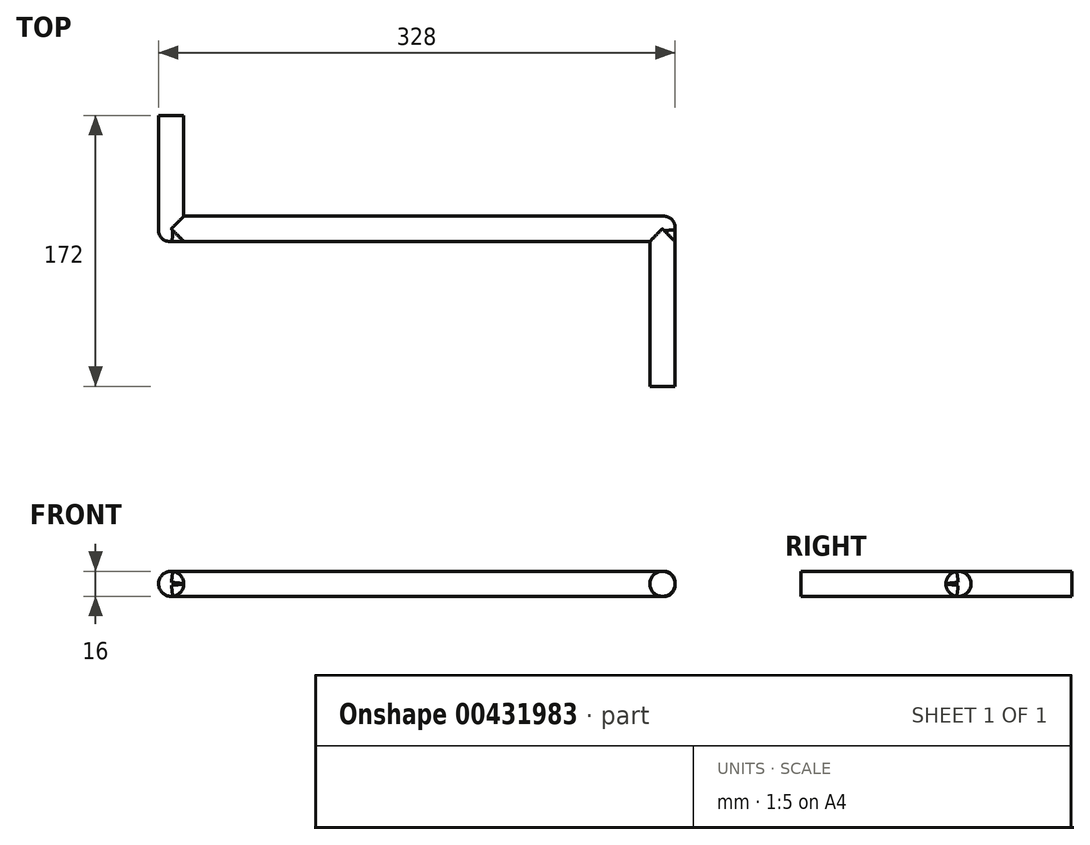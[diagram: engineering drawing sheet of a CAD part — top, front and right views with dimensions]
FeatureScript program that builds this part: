
annotation { "Feature Type Name" : "Feature", "Feature Type Description" : "" }
export const myFeature = defineFeature(function(context is Context, id is Id, definition is map)
    precondition{}
    {
        {
            var Q0;
            Q0=qCreatedBy(makeId("Front.planeOp"),FACE);
            var sketch = newSketch(context, id + "F0", { "sketchPlane" : qUnion([Q0])});
            skCircle(sketch, "E0", {"center": v(0, 0) * mm, "radius": 8 * mm});
            skSolve(sketch);
        }
        {
            var Q0;
            Q0=qSketchRegion(id+"F0",true);
            extrude(context, id + "F1", {"entities" : qUnion([Q0]), "depth" : 80 * mm});
        }
        {
            var Q0;
            Q0=qCreatedBy(makeId("Right.planeOp"),FACE);
            var sketch = newSketch(context, id + "F2", { "sketchPlane" : qUnion([Q0])});
            skCircle(sketch, "E1", {"center": v(-72, 0) * mm, "radius": 8 * mm});
            skSolve(sketch);
        }
        {
            var Q0;
            Q0=qSketchRegion(id+"F2",true);
            extrude(context, id + "F3", {"entities" : qUnion([Q0]), "operationType" : NewBodyOperationType.ADD, "depth" : 320 * mm, "offsetDistance" : 25 * mm});
        }
        {
            var Q0;
            Q0=qCreatedBy(makeId("Front.planeOp"),FACE);
            cPlane(context, id + "F4", {"entities" : qUnion([Q0]), "cplaneType" : CPlaneType.OFFSET, "offset" : 72 * mm, "width" : 150 * mm, "height" : 150 * mm});
        }
        {
            var Q0;
            Q0=qCreatedBy(id+"F4.planeOp",FACE);
            var sketch = newSketch(context, id + "F5", { "sketchPlane" : qUnion([Q0])});
            skCircle(sketch, "E2", {"center": v(312, 0) * mm, "radius": 8 * mm});
            skSolve(sketch);
        }
        {
            var Q0;
            Q0=qSketchRegion(id+"F5",true);
            extrude(context, id + "F6", {"entities" : qUnion([Q0]), "operationType" : NewBodyOperationType.ADD, "depth" : 100 * mm});
        }
        {
            var Q0;
            Q0=makeQuery(id+"F3.opExtrude","CAP_EDGE",EDGE,{"disambiguationData":[OSD([sQuery(id+"F2.wireOp",EDGE,"E1")])],"isStart":false});
            fillet(context, id + "F7", {"entities" : qUnion([Q0]), "radius" : 7 * mm, "tangentPropagation" : true, "allowEdgeOverflow" : false});
        }
        {
            var Q0;
            Q0=makeQuery(id+"F1.opExtrude","CAP_EDGE",EDGE,{"disambiguationData":[OSD([sQuery(id+"F0.wireOp",EDGE,"E0")])],"isStart":false});
            fillet(context, id + "F8", {"entities" : qUnion([Q0]), "radius" : 7 * mm, "tangentPropagation" : true, "allowEdgeOverflow" : false});
        }
    });
